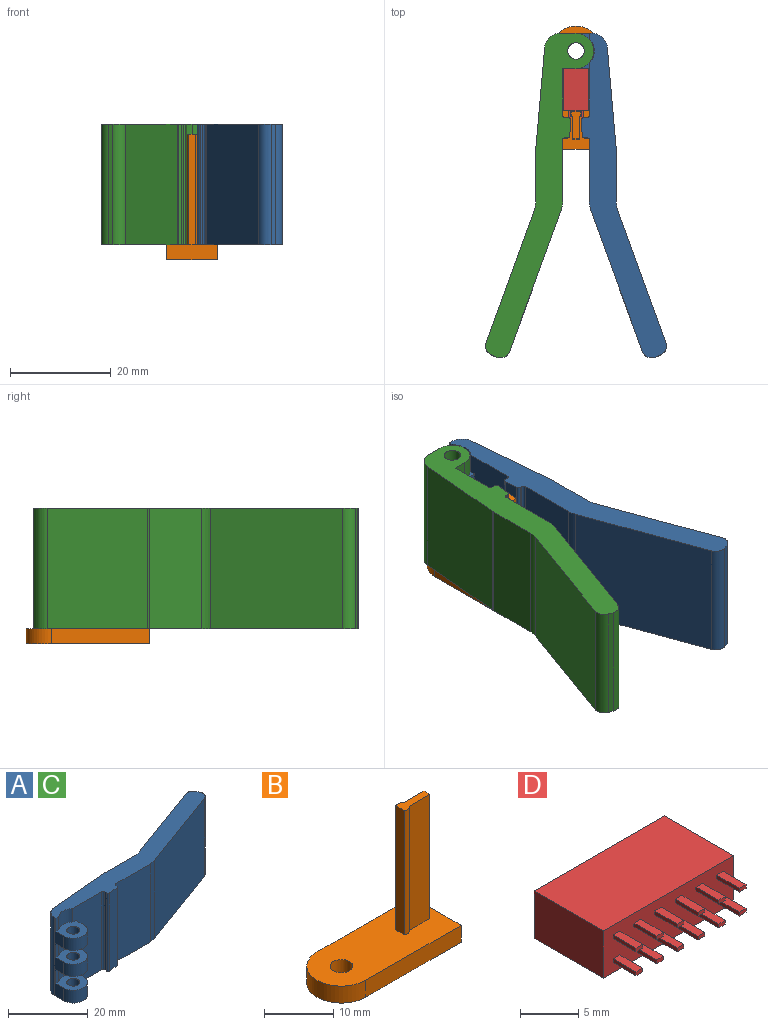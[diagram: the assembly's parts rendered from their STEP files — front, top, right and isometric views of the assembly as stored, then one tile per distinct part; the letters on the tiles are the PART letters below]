
ASSEMBLY  parts=4 mates=2
PART A: 43 faces, bbox 64.5x21.5x24 mm
  f0: plane 24x10.32mm, normal (0,-1,0), area 235.9mm2, adj f3,f4,f10,f12,f31,f32,f33,f34
  f1: plane 4.2x1.02mm, normal (0,-1,0), area 4.3mm2, adj f9,f33,f34,f42
  f2: plane 4.1x1.02mm, normal (0,-1,0), area 4.2mm2, adj f9,f31,f39,f40
  f3: plane 3.8x2.68mm, normal (1,0,0), area 10.2mm2, adj f0,f5,f35,f39
  f4: plane 3.8x2.68mm, normal (1,0,0), area 10.2mm2, adj f0,f6,f34,f36
  f5: cylinder r=3.5mm len=7mm, axis (0,0,-1), area 41.8mm2, adj f3,f9,f35,f39
  f6: cylinder r=3.5mm len=7mm, axis (0,0,-1), area 41.8mm2, adj f4,f9,f34,f36
  f7: cylinder r=3.5mm len=7mm, axis (0,0,-1), area 42.9mm2, adj f9,f10,f32,f33
  f8: cylinder r=1.65mm len=3.9mm, axis (0,0,-1), area 40.4mm2, adj f32,f33
  f9: plane 24x3.25mm, normal (-1,0,0), area 44.4mm2, adj f1,f2,f5,f6,f7,f11,f30,f31
  f10: plane 3.9x2.68mm, normal (1,0,0), area 10.4mm2, adj f0,f7,f32,f33
  f11: plane 4.2x1.02mm, normal (0,-1,0), area 4.3mm2, adj f9,f35,f36,f41
  f12: cylinder r=0.5mm len=24mm, axis (0,0,-1), area 18.8mm2, adj f0,f13,f31,f32
  f13: plane 24x0.68mm, normal (-1,0,0), area 16.2mm2, adj f12,f14,f31,f32
  f14: cylinder r=0.5mm len=24mm, axis (0,0,-1), area 19.9mm2, adj f13,f15,f31,f32
  f15: plane 24x3mm, normal (0.09,-1,0), area 72.3mm2, adj f14,f16,f31,f32
  f16: cylinder r=0.5mm len=24mm, axis (0,0,-1), area 17.8mm2, adj f15,f17,f31,f32
  f17: plane 24x0.41mm, normal (1,0,0), area 9.9mm2, adj f16,f18,f31,f32
  f18: cylinder r=0.5mm len=24mm, axis (0,0,-1), area 18.8mm2, adj f17,f19,f31,f32
  f19: plane 24x12.2mm, normal (0,-1,0), area 292.8mm2, adj f18,f20,f31,f32
  f20: cylinder r=5mm len=24mm, axis (0,0,-1), area 41.9mm2, adj f19,f21,f31,f32
  f21: plane 28.02x24mm, normal (0.34,-0.94,0), area 715.7mm2, adj f20,f22,f31,f32
  f22: cylinder r=2mm len=24mm, axis (0,0,-1), area 75.4mm2, adj f21,f23,f31,f32
  f23: plane 24x0.94mm, normal (0.94,0.34,0), area 24mm2, adj f22,f24,f31,f32
  f24: cylinder r=2mm len=24mm, axis (0,0,-1), area 75.4mm2, adj f23,f25,f31,f32
  f25: plane 26.31x24mm, normal (-0.34,0.94,0), area 672mm2, adj f24,f26,f31,f32
  f26: cylinder r=5mm len=24mm, axis (0,0,-1), area 41.9mm2, adj f25,f27,f31,f32
  f27: plane 24x10.4mm, normal (0,1,0), area 249.6mm2, adj f26,f28,f31,f32
  f28: cylinder r=5mm len=24mm, axis (0,0,-1), area 10.5mm2, adj f27,f29,f31,f32
  f29: plane 24x19.92mm, normal (-0.09,1,0), area 480mm2, adj f28,f30,f31,f32
  f30: cylinder r=3mm len=24mm, axis (0,0,-1), area 106.8mm2, adj f9,f29,f31,f32
  f31: plane 64.55x17mm, normal (0,0,1), area 318.6mm2, adj f0,f2,f9,f12,f13,f14,f15,f16
  f32: plane 64.55x21.49mm, normal (0,0,-1), area 351.3mm2, adj f0,f7,f8,f9,f10,f12,f13,f14
  f33: plane 7.15x7mm, normal (0,0,1), area 32.7mm2, adj f0,f1,f7,f8,f9,f10,f42
  f34: plane 7.15x7mm, normal (0,0,-1), area 32.7mm2, adj f0,f1,f4,f6,f9,f37,f42
  f35: plane 7.15x7mm, normal (0,0,-1), area 32.7mm2, adj f0,f3,f5,f9,f11,f38,f41
  f36: plane 7.15x7mm, normal (0,0,1), area 32.7mm2, adj f0,f4,f6,f9,f11,f37,f41
  f37: cylinder r=1.65mm len=3.8mm, axis (0,0,-1), area 39.4mm2, adj f34,f36
  f38: cylinder r=1.65mm len=3.8mm, axis (0,0,-1), area 39.4mm2, adj f35,f39
  f39: plane 7.15x7mm, normal (0,0,1), area 32.7mm2, adj f0,f2,f3,f5,f9,f38,f40
  f40: cylinder r=3.65mm len=4.97mm, axis (0,0,1), area 22.4mm2, adj f0,f2,f31,f39
  f41: cylinder r=3.65mm len=4.97mm, axis (0,0,-1), area 22.9mm2, adj f0,f11,f35,f36
  f42: cylinder r=3.65mm len=4.97mm, axis (0,0,-1), area 22.9mm2, adj f0,f1,f33,f34
PART B: 14 faces, bbox 24.5x10x25 mm
  f0: cylinder r=1mm len=22mm, axis (0,0,-1), area 31.8mm2, adj f1,f5,f6,f12
  f1: plane 22x4.2mm, normal (0,-1,0), area 92.4mm2, adj f0,f2,f6,f12
  f2: plane 22x1.2mm, normal (1,0,0), area 26.4mm2, adj f1,f3,f6,f12
  f3: plane 22x4.2mm, normal (0,1,0), area 92.4mm2, adj f2,f4,f6,f12
  f4: cylinder r=1mm len=22mm, axis (0,0,-1), area 31.8mm2, adj f3,f5,f6,f12
  f5: plane 22x1.74mm, normal (-1,0,0), area 38.2mm2, adj f0,f4,f6,f12
  f6: plane 5.5x2mm, normal (0,0,1), area 7.4mm2, adj f0,f1,f2,f3,f4,f5
  f7: plane 19.5x3mm, normal (0,-1,0), area 58.5mm2, adj f8,f10,f12,f13
  f8: cylinder r=5mm len=10mm, axis (0,0,-1), area 47.1mm2, adj f7,f9,f12,f13
  f9: plane 19.5x3mm, normal (0,1,0), area 58.5mm2, adj f8,f10,f12,f13
  f10: plane 10x3mm, normal (1,0,0), area 30mm2, adj f7,f9,f12,f13
  f11: cylinder r=1.65mm len=3.3mm, axis (0,0,-1), area 31.1mm2, adj f12,f13
  f12: plane 24.5x10mm, normal (0,0,1), area 218.3mm2, adj f0,f1,f2,f3,f4,f5,f7,f8
  f13: plane 24.5x10mm, normal (0,0,-1), area 225.7mm2, adj f7,f8,f9,f10,f11
PART C: same geometry as A
PART D: 66 faces, bbox 15.7x11.1x5 mm
  f0: plane 15.74x4.95mm, normal (0,-1,0), area 74.1mm2, adj f1,f2,f4,f5,f6,f7,f8,f9
  f1: plane 8.36x4.95mm, normal (-1,0,0), area 41.4mm2, adj f0,f3,f4,f5
  f2: plane 8.36x4.95mm, normal (1,0,0), area 41.4mm2, adj f0,f3,f4,f5
  f3: plane 15.74x4.95mm, normal (0,1,0), area 77.9mm2, adj f1,f2,f4,f5
  f4: plane 15.74x8.36mm, normal (0,0,1), area 131.6mm2, adj f0,f1,f2,f3
  f5: plane 15.74x8.36mm, normal (0,0,-1), area 131.6mm2, adj f0,f1,f2,f3
  f6: plane 2.75x0.8mm, normal (0,0,1), area 2.2mm2, adj f0,f7,f9,f10
  f7: plane 2.75x0.4mm, normal (-1,0,0), area 1.1mm2, adj f0,f6,f8,f10
  f8: plane 2.75x0.8mm, normal (0,0,-1), area 2.2mm2, adj f0,f7,f9,f10
  f9: plane 2.75x0.4mm, normal (1,0,0), area 1.1mm2, adj f0,f6,f8,f10
  f10: plane 0.8x0.4mm, normal (0,-1,0), area 0.3mm2, adj f6,f7,f8,f9
  f11: plane 2.75x0.8mm, normal (0,0,1), area 2.2mm2, adj f0,f12,f14,f15
  f12: plane 2.75x0.4mm, normal (-1,0,0), area 1.1mm2, adj f0,f11,f13,f15
  f13: plane 2.75x0.8mm, normal (0,0,-1), area 2.2mm2, adj f0,f12,f14,f15
  f14: plane 2.75x0.4mm, normal (1,0,0), area 1.1mm2, adj f0,f11,f13,f15
  f15: plane 0.8x0.4mm, normal (0,-1,0), area 0.3mm2, adj f11,f12,f13,f14
  f16: plane 2.75x0.4mm, normal (1,0,0), area 1.1mm2, adj f0,f17,f19,f20
  f17: plane 2.75x0.8mm, normal (0,0,1), area 2.2mm2, adj f0,f16,f18,f20
  f18: plane 2.75x0.4mm, normal (-1,0,0), area 1.1mm2, adj f0,f17,f19,f20
  f19: plane 2.75x0.8mm, normal (0,0,-1), area 2.2mm2, adj f0,f16,f18,f20
  f20: plane 0.8x0.4mm, normal (0,-1,0), area 0.3mm2, adj f16,f17,f18,f19
  f21: plane 2.75x0.4mm, normal (-1,0,0), area 1.1mm2, adj f0,f22,f24,f25
  f22: plane 2.75x0.8mm, normal (0,0,-1), area 2.2mm2, adj f0,f21,f23,f25
  f23: plane 2.75x0.4mm, normal (1,0,0), area 1.1mm2, adj f0,f22,f24,f25
  f24: plane 2.75x0.8mm, normal (0,0,1), area 2.2mm2, adj f0,f21,f23,f25
  f25: plane 0.8x0.4mm, normal (0,-1,0), area 0.3mm2, adj f21,f22,f23,f24
  f26: plane 2.75x0.8mm, normal (0,0,1), area 2.2mm2, adj f0,f27,f29,f30
  f27: plane 2.75x0.4mm, normal (-1,0,0), area 1.1mm2, adj f0,f26,f28,f30
  f28: plane 2.75x0.8mm, normal (0,0,-1), area 2.2mm2, adj f0,f27,f29,f30
  f29: plane 2.75x0.4mm, normal (1,0,0), area 1.1mm2, adj f0,f26,f28,f30
  f30: plane 0.8x0.4mm, normal (0,-1,0), area 0.3mm2, adj f26,f27,f28,f29
  f31: plane 2.75x0.8mm, normal (0,0,1), area 2.2mm2, adj f0,f32,f34,f35
  f32: plane 2.75x0.4mm, normal (-1,0,0), area 1.1mm2, adj f0,f31,f33,f35
  f33: plane 2.75x0.8mm, normal (0,0,-1), area 2.2mm2, adj f0,f32,f34,f35
  f34: plane 2.75x0.4mm, normal (1,0,0), area 1.1mm2, adj f0,f31,f33,f35
  f35: plane 0.8x0.4mm, normal (0,-1,0), area 0.3mm2, adj f31,f32,f33,f34
  f36: plane 2.75x0.4mm, normal (-1,0,0), area 1.1mm2, adj f0,f37,f39,f40
  f37: plane 2.75x0.8mm, normal (0,0,-1), area 2.2mm2, adj f0,f36,f38,f40
  f38: plane 2.75x0.4mm, normal (1,0,0), area 1.1mm2, adj f0,f37,f39,f40
  f39: plane 2.75x0.8mm, normal (0,0,1), area 2.2mm2, adj f0,f36,f38,f40
  f40: plane 0.8x0.4mm, normal (0,-1,0), area 0.3mm2, adj f36,f37,f38,f39
  f41: plane 2.75x0.4mm, normal (-1,0,0), area 1.1mm2, adj f0,f42,f44,f45
  f42: plane 2.75x0.8mm, normal (0,0,-1), area 2.2mm2, adj f0,f41,f43,f45
  f43: plane 2.75x0.4mm, normal (1,0,0), area 1.1mm2, adj f0,f42,f44,f45
  f44: plane 2.75x0.8mm, normal (0,0,1), area 2.2mm2, adj f0,f41,f43,f45
  f45: plane 0.8x0.4mm, normal (0,-1,0), area 0.3mm2, adj f41,f42,f43,f44
  f46: plane 2.75x0.4mm, normal (-1,0,0), area 1.1mm2, adj f0,f47,f49,f50
  f47: plane 2.75x0.8mm, normal (0,0,-1), area 2.2mm2, adj f0,f46,f48,f50
  f48: plane 2.75x0.4mm, normal (1,0,0), area 1.1mm2, adj f0,f47,f49,f50
  f49: plane 2.75x0.8mm, normal (0,0,1), area 2.2mm2, adj f0,f46,f48,f50
  f50: plane 0.8x0.4mm, normal (0,-1,0), area 0.3mm2, adj f46,f47,f48,f49
  f51: plane 2.75x0.4mm, normal (-1,0,0), area 1.1mm2, adj f0,f52,f54,f55
  f52: plane 2.75x0.8mm, normal (0,0,-1), area 2.2mm2, adj f0,f51,f53,f55
  f53: plane 2.75x0.4mm, normal (1,0,0), area 1.1mm2, adj f0,f52,f54,f55
  f54: plane 2.75x0.8mm, normal (0,0,1), area 2.2mm2, adj f0,f51,f53,f55
  f55: plane 0.8x0.4mm, normal (0,-1,0), area 0.3mm2, adj f51,f52,f53,f54
  f56: plane 2.75x0.8mm, normal (0,0,1), area 2.2mm2, adj f0,f57,f59,f60
  f57: plane 2.75x0.4mm, normal (-1,0,0), area 1.1mm2, adj f0,f56,f58,f60
  f58: plane 2.75x0.8mm, normal (0,0,-1), area 2.2mm2, adj f0,f57,f59,f60
  f59: plane 2.75x0.4mm, normal (1,0,0), area 1.1mm2, adj f0,f56,f58,f60
  f60: plane 0.8x0.4mm, normal (0,-1,0), area 0.3mm2, adj f56,f57,f58,f59
  f61: plane 2.75x0.4mm, normal (-1,0,0), area 1.1mm2, adj f0,f62,f64,f65
  f62: plane 2.75x0.8mm, normal (0,0,-1), area 2.2mm2, adj f0,f61,f63,f65
  f63: plane 2.75x0.4mm, normal (1,0,0), area 1.1mm2, adj f0,f62,f64,f65
  f64: plane 2.75x0.8mm, normal (0,0,1), area 2.2mm2, adj f0,f61,f63,f65
  f65: plane 0.8x0.4mm, normal (0,-1,0), area 0.3mm2, adj f61,f62,f63,f64
PLACE A rot(axis=(0,0,-1),90deg) t=(0,0,0)mm
PLACE B rot(axis=(0,0,-1),90deg) t=(0,-12.5,-3)mm
PLACE C rot(axis=(0.71,-0.71,0),180deg) t=(0,0,24)mm
PLACE D rot(axis=(0,1,0),90deg) t=(-2.47,-11.86,17.74)mm
MATE fastened A.f10 <-> D.f3  axis (0,-1,0) through (2.67,-3.5,0)mm
MATE fastened A.f8 <-> B.f11  axis (0,0,-1) through (0,0,0)mm
